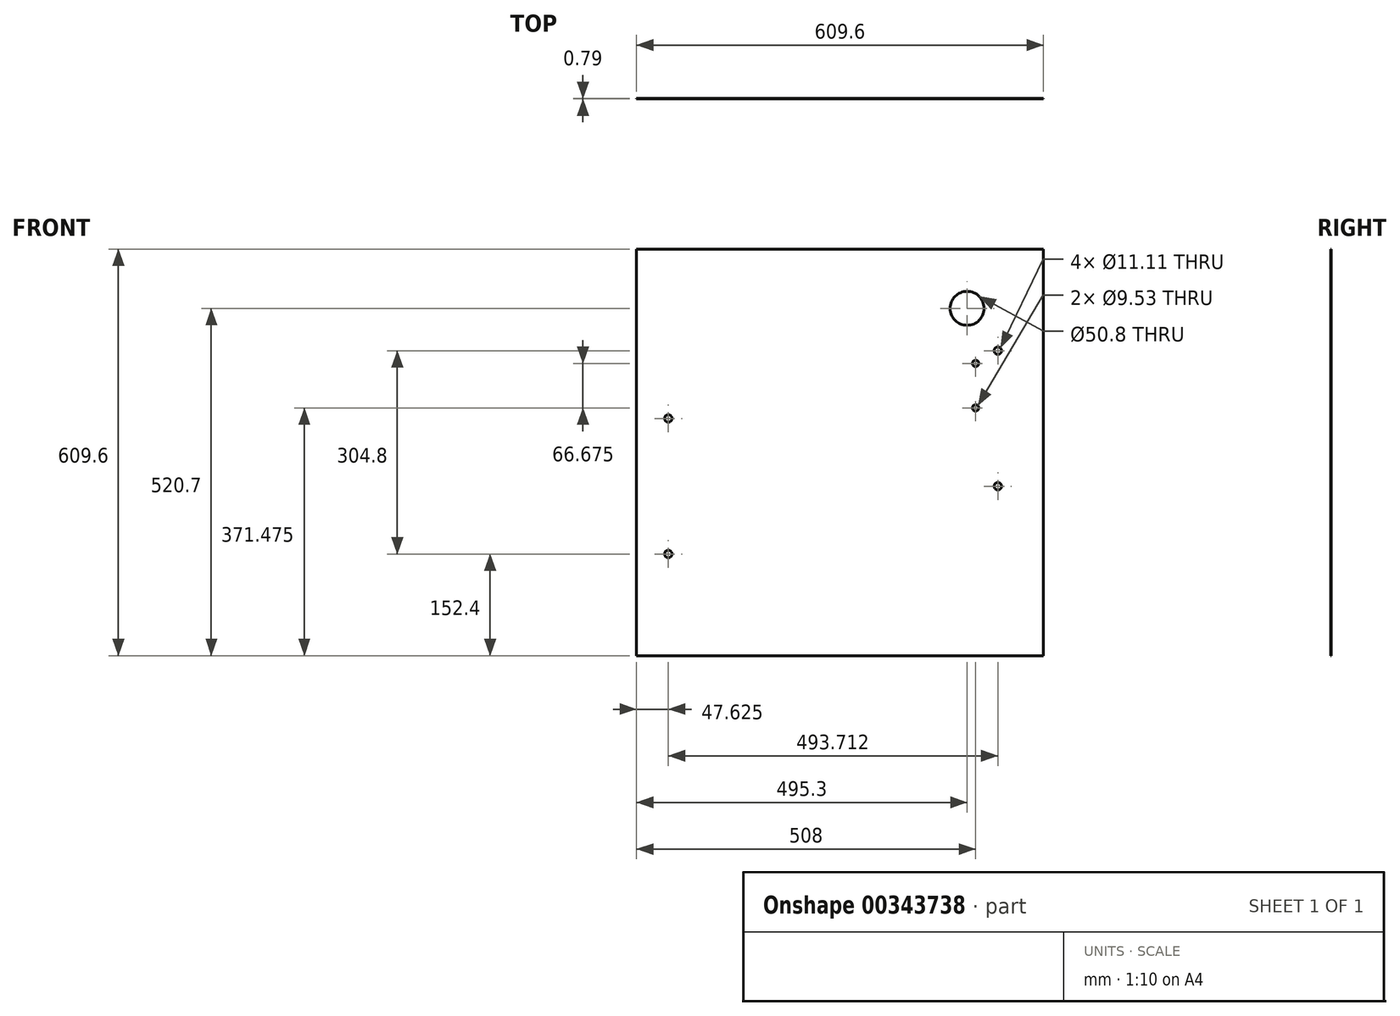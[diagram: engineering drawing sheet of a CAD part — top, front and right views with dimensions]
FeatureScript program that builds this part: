
annotation { "Feature Type Name" : "Feature", "Feature Type Description" : "" }
export const myFeature = defineFeature(function(context is Context, id is Id, definition is map)
    precondition{}
    {
        {
            var Q0;
            Q0=qCreatedBy(makeId("Front.planeOp"),FACE);
            var sketch = newSketch(context, id + "F0", { "sketchPlane" : qUnion([Q0])});
            skLineSegment(sketch, "E0.bottom", {"start": v(0, 0) * mm, "end": v(609.6, 0) * mm});
            skLineSegment(sketch, "E0.top", {"start": v(0, 609.6) * mm, "end": v(609.6, 609.6) * mm});
            skLineSegment(sketch, "E0.left", {"start": v(0, 0) * mm, "end": v(0, 609.6) * mm});
            skLineSegment(sketch, "E0.right", {"start": v(609.6, 0) * mm, "end": v(609.6, 609.6) * mm});
            skSolve(sketch);
        }
        {
            var Q0;
            Q0=makeQuery(id+"F0.imprint","IMPRINT",FACE,{"disambiguationData":[TD([[makeQuery(id+"F0.imprint","IMPRINT",EDGE,{"derivedFrom":sQuery(id+"F0.wireOp",EDGE,"E0.top")}),-1.0]])]});
            extrude(context, id + "F1", {"entities" : qUnion([Q0]), "depth" : 0.8 * mm});
        }
        {
            var Q0;
            Q0=makeQuery(id+"F1.opExtrude","CAP_FACE",FACE,{"disambiguationData":[OSD([sQuery(id+"F0.wireOp",EDGE,"E0.bottom"),sQuery(id+"F0.wireOp",EDGE,"E0.top"),sQuery(id+"F0.wireOp",EDGE,"E0.left"),sQuery(id+"F0.wireOp",EDGE,"E0.right")])],"isStart":false});
            var sketch = newSketch(context, id + "F2", { "sketchPlane" : qUnion([Q0])});
            skCircle(sketch, "E1", {"center": v(47.63, 152.4) * mm, "radius": 5.56 * mm});
            skCircle(sketch, "E2", {"center": v(47.62, 355.6) * mm, "radius": 5.56 * mm});
            skCircle(sketch, "E3", {"center": v(541.34, 457.2) * mm, "radius": 5.56 * mm});
            skCircle(sketch, "E4", {"center": v(541.34, 254) * mm, "radius": 5.56 * mm});
            skSolve(sketch);
        }
        {
            var Q0;
            Q0=makeQuery(id+"F2.imprint","IMPRINT",FACE,{"disambiguationData":[TD([[makeQuery(id+"F2.imprint","IMPRINT",EDGE,{"derivedFrom":sQuery(id+"F2.wireOp",EDGE,"E2")}),1.0]])]});
            var Q1;
            Q1=makeQuery(id+"F2.imprint","IMPRINT",FACE,{"disambiguationData":[TD([[makeQuery(id+"F2.imprint","IMPRINT",EDGE,{"derivedFrom":sQuery(id+"F2.wireOp",EDGE,"E1")}),1.0]])]});
            var Q2;
            Q2=makeQuery(id+"F2.imprint","IMPRINT",FACE,{"disambiguationData":[TD([[makeQuery(id+"F2.imprint","IMPRINT",EDGE,{"derivedFrom":sQuery(id+"F2.wireOp",EDGE,"E4")}),1.0]])]});
            var Q3;
            Q3=makeQuery(id+"F2.imprint","IMPRINT",FACE,{"disambiguationData":[TD([[makeQuery(id+"F2.imprint","IMPRINT",EDGE,{"derivedFrom":sQuery(id+"F2.wireOp",EDGE,"E3")}),1.0]])]});
            extrude(context, id + "F3", {"entities" : qUnion([Q0, Q1, Q2, Q3]), "operationType" : NewBodyOperationType.REMOVE, "oppositeDirection" : true, "depth" : 25.4 * mm});
        }
        {
            var Q0;
            Q0=makeQuery(id+"F1.opExtrude","CAP_FACE",FACE,{"disambiguationData":[OSD([sQuery(id+"F0.wireOp",EDGE,"E0.bottom"),sQuery(id+"F0.wireOp",EDGE,"E0.top"),sQuery(id+"F0.wireOp",EDGE,"E0.left"),sQuery(id+"F0.wireOp",EDGE,"E0.right")])],"isStart":false});
            var sketch = newSketch(context, id + "F4", { "sketchPlane" : qUnion([Q0])});
            skLineSegment(sketch, "E5", {"start": v(0, 561.97) * mm, "end": v(609.6, 561.98) * mm, "construction": true});
            skLineSegment(sketch, "E6", {"start": v(561.97, 609.6) * mm, "end": v(561.98, 0) * mm, "construction": true});
            skCircle(sketch, "E7", {"center": v(495.3, 520.7) * mm, "radius": 25.4 * mm});
            skCircle(sketch, "E8", {"center": v(541.34, 457.2) * mm, "radius": 5.56 * mm, "construction": true});
            skLineSegment(sketch, "E9", {"start": v(508, 609.6) * mm, "end": v(508, 0) * mm, "construction": true});
            skCircle(sketch, "E10", {"center": v(508, 438.15) * mm, "radius": 4.76 * mm});
            skCircle(sketch, "E11", {"center": v(508, 371.48) * mm, "radius": 4.76 * mm});
            skSolve(sketch);
        }
        {
            var Q0;
            Q0=makeQuery(id+"F4.imprint","IMPRINT",FACE,{"disambiguationData":[TD([[makeQuery(id+"F4.imprint","IMPRINT",EDGE,{"derivedFrom":sQuery(id+"F4.wireOp",EDGE,"E7")}),1.0]])]});
            var Q1;
            Q1=makeQuery(id+"F4.imprint","IMPRINT",FACE,{"disambiguationData":[TD([[makeQuery(id+"F4.imprint","IMPRINT",EDGE,{"derivedFrom":sQuery(id+"F4.wireOp",EDGE,"dIs04lKC-0cYj-xAZQ-mJBj-wLfXOmUrUEd0")}),1.0]])]});
            var Q2;
            Q2=makeQuery(id+"F4.imprint","IMPRINT",FACE,{"disambiguationData":[TD([[makeQuery(id+"F4.imprint","IMPRINT",EDGE,{"derivedFrom":sQuery(id+"F4.wireOp",EDGE,"PuCWZrF6-xYAN-FH2s-6trX-rO64wnm37StW")}),1.0]])]});
            var Q3;
            Q3=makeQuery(id+"F4.imprint","IMPRINT",FACE,{"disambiguationData":[TD([[makeQuery(id+"F4.imprint","IMPRINT",EDGE,{"derivedFrom":sQuery(id+"F4.wireOp",EDGE,"cdf4c5bd-17c5-4b4c-997a-f66c13169bcd.0.1.1")}),1.0]])]});
            var Q4;
            Q4=makeQuery(id+"F4.imprint","IMPRINT",FACE,{"disambiguationData":[TD([[makeQuery(id+"F4.imprint","IMPRINT",EDGE,{"derivedFrom":sQuery(id+"F4.wireOp",EDGE,"cdf4c5bd-17c5-4b4c-997a-f66c13169bcd.0.2.1")}),1.0]])]});
            var Q5;
            Q5=makeQuery(id+"F4.imprint","IMPRINT",FACE,{"disambiguationData":[TD([[makeQuery(id+"F4.imprint","IMPRINT",EDGE,{"derivedFrom":sQuery(id+"F4.wireOp",EDGE,"cdf4c5bd-17c5-4b4c-997a-f66c13169bcd.0.2.0")}),1.0]])]});
            var Q6;
            Q6=makeQuery(id+"F4.imprint","IMPRINT",FACE,{"disambiguationData":[TD([[makeQuery(id+"F4.imprint","IMPRINT",EDGE,{"derivedFrom":sQuery(id+"F4.wireOp",EDGE,"cdf4c5bd-17c5-4b4c-997a-f66c13169bcd.0.1.0")}),1.0]])]});
            var Q7;
            Q7=makeQuery(id+"F4.imprint","IMPRINT",FACE,{"disambiguationData":[TD([[makeQuery(id+"F4.imprint","IMPRINT",EDGE,{"derivedFrom":sQuery(id+"F4.wireOp",EDGE,"E10")}),1.0]])]});
            var Q8;
            Q8=makeQuery(id+"F4.imprint","IMPRINT",FACE,{"disambiguationData":[TD([[makeQuery(id+"F4.imprint","IMPRINT",EDGE,{"derivedFrom":sQuery(id+"F4.wireOp",EDGE,"E11")}),1.0]])]});
            extrude(context, id + "F5", {"entities" : qUnion([Q0, Q1, Q2, Q3, Q4, Q5, Q6, Q7, Q8]), "operationType" : NewBodyOperationType.REMOVE, "oppositeDirection" : true, "depth" : 25.4 * mm});
        }
    });
